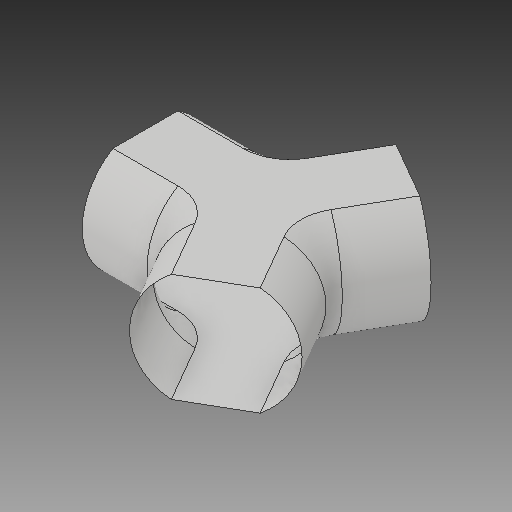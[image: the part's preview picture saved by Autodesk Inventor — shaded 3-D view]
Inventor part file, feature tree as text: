
AUTODESK INVENTOR PART (.ipt)
format: ipt  version: 2017 (Build 210142000, 142)  size: 192,000 bytes
history: native  units: in
note: dims shown in document units (in); Inventor stores cm internally (conversion verified against a paired STEP export)
features: sketch x3, extrude x2, other x2, pattern_circular x2, sweep x1, delete_face x1
ambient origin geometry x8: Origin, YZ Plane, XZ Plane, XY Plane, X Axis, Y Axis, Z Axis, Center Point
bodies: Solid1 (feature_tree)
feature tree (11):
  sketch  "Sketch1"  dims[d10=6.6667in d12=4.0in d13=0.0in d15=2.8217in d16=1.1811in d17=360.0deg]
  extrude  "corridor"  Depth=6.6667in
  other  "found rotaion axis"
  other  "rotaion axis"
  pattern_circular  "other corridors"  Count=3 Angle=360.0deg
  sketch  "Sketch5"  dims[d105=4.0in d107=3.8873in d108=3.8873in d112=1.6458in d118=3.3333in d120=1.0in d121=0.0in]
  sketch  "Sketch4"  dims[d24=0.0in d25=0.0in d26=1.1811in d27=360.0deg]
  sweep  "curve edjes"
  pattern_circular  "repeat curve edjes"  [2 undecoded]
  extrude  "hole fill in"  [1 undecoded]
  delete_face  "Delete Face1"
note: 3 required parameter values undecoded (feature->parameter linkage not recoverable at this tier; creation-order binding heuristic only, values carry confidence <= 0.55)
